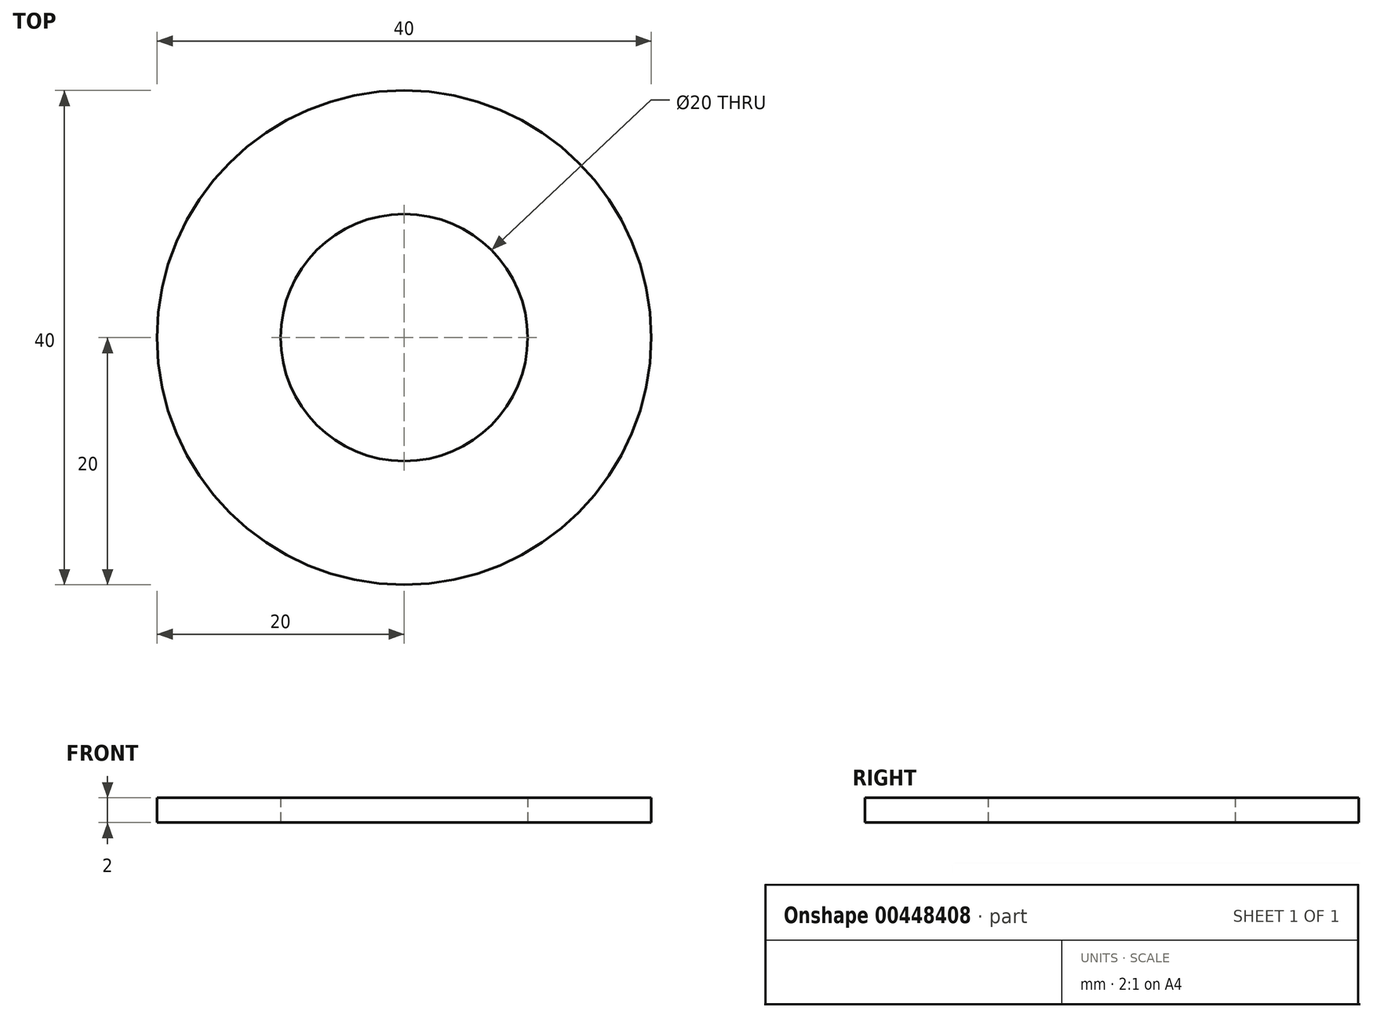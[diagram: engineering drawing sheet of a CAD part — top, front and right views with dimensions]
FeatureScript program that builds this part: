
annotation { "Feature Type Name" : "Feature", "Feature Type Description" : "" }
export const myFeature = defineFeature(function(context is Context, id is Id, definition is map)
    precondition{}
    {
        {
            var Q0;
            Q0=qCreatedBy(makeId("Top.planeOp"),FACE);
            var sketch = newSketch(context, id + "F0", { "sketchPlane" : qUnion([Q0])});
            skCircle(sketch, "E0", {"center": v(0, 0) * mm, "radius": 10 * mm});
            skCircle(sketch, "E1", {"center": v(0, 0) * mm, "radius": 20 * mm});
            skSolve(sketch);
        }
        {
            var Q0;
            Q0 = qSketchRegion(id + "F0", true);
            extrude(context, id + "F1", {"entities" : qUnion([Q0]), "depth" : 2 * mm});
        }
    });
